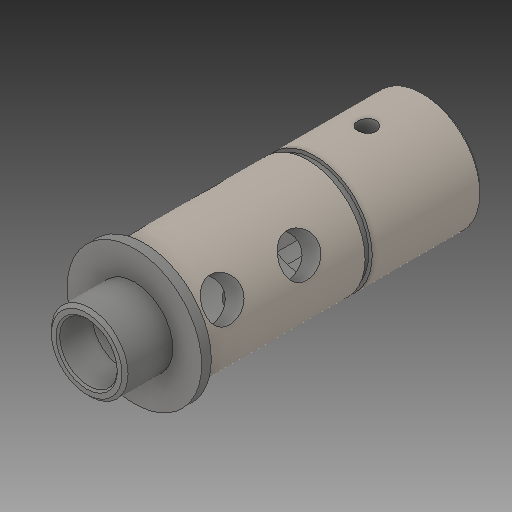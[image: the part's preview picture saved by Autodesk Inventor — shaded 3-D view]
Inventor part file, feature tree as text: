
AUTODESK INVENTOR PART (.ipt)
format: ipt  version: 2017 (Build 210142000, 142)  size: 239,104 bytes
history: native  units: in
note: dims shown in document units (in); Inventor stores cm internally (conversion verified against a paired STEP export)
features: chamfer x1
ambient origin geometry x8: Origin, YZ Plane, XZ Plane, XY Plane, X Axis, Y Axis, Z Axis, Center Point
bodies: Solid1 (feature_tree)
feature tree (1):
  chamfer  "Chamfer4"  [1 undecoded]
note: 1 required parameter value undecoded (feature->parameter linkage not recoverable at this tier; creation-order binding heuristic only, values carry confidence <= 0.55)
